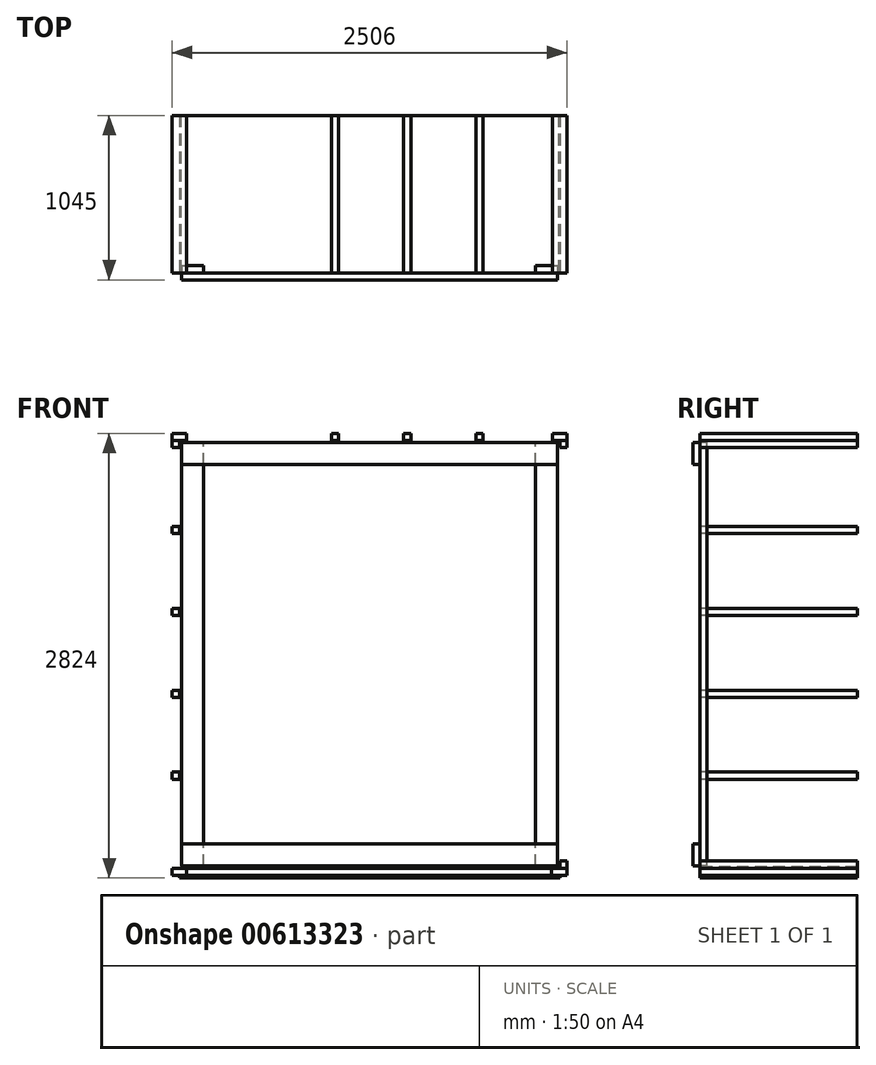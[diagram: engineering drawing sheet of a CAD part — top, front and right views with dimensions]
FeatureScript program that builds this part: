
annotation { "Feature Type Name" : "Feature", "Feature Type Description" : "" }
export const myFeature = defineFeature(function(context is Context, id is Id, definition is map)
    precondition{}
    {
        {
            var Q0;
            Q0=qCreatedBy(makeId("Front.planeOp"),FACE);
            var sketch = newSketch(context, id + "F0", { "sketchPlane" : qUnion([Q0])});
            skLineSegment(sketch, "E0.bottom", {"start": v(0, 0) * mm, "end": v(2400, 0) * mm});
            skLineSegment(sketch, "E0.top", {"start": v(0, 2700) * mm, "end": v(2400, 2700) * mm});
            skLineSegment(sketch, "E0.left", {"start": v(0, 0) * mm, "end": v(0, 2700) * mm});
            skLineSegment(sketch, "E0.right", {"start": v(2400, 0) * mm, "end": v(2400, 2700) * mm});
            skLineSegment(sketch, "E1.0", {"start": v(145, 2555) * mm, "end": v(2255, 2555) * mm});
            skLineSegment(sketch, "E1.1", {"start": v(145, 145) * mm, "end": v(145, 2555) * mm});
            skLineSegment(sketch, "E1.2", {"start": v(145, 145) * mm, "end": v(2255, 145) * mm});
            skLineSegment(sketch, "E1.3", {"start": v(2255, 145) * mm, "end": v(2255, 2555) * mm});
            skLineSegment(sketch, "E2.0", {"start": v(167, 167) * mm, "end": v(167, 2533) * mm});
            skLineSegment(sketch, "E2.1", {"start": v(167, 167) * mm, "end": v(2233, 167) * mm});
            skLineSegment(sketch, "E2.2", {"start": v(2233, 167) * mm, "end": v(2233, 2533) * mm});
            skLineSegment(sketch, "E2.3", {"start": v(167, 2533) * mm, "end": v(2233, 2533) * mm});
            skLineSegment(sketch, "E3", {"start": v(145, 2555) * mm, "end": v(0, 2555) * mm});
            skLineSegment(sketch, "E4", {"start": v(145, 2555) * mm, "end": v(145, 2700) * mm});
            skLineSegment(sketch, "E5", {"start": v(2255, 2555) * mm, "end": v(2255, 2700) * mm});
            skLineSegment(sketch, "E6", {"start": v(2255, 2555) * mm, "end": v(2400, 2555) * mm});
            skLineSegment(sketch, "E7", {"start": v(145, 145) * mm, "end": v(145, 0) * mm});
            skLineSegment(sketch, "E8", {"start": v(145, 145) * mm, "end": v(0, 145) * mm});
            skLineSegment(sketch, "E9", {"start": v(2255, 145) * mm, "end": v(2400, 145) * mm});
            skLineSegment(sketch, "E10", {"start": v(2255, 145) * mm, "end": v(2255, 0) * mm});
            skLineSegment(sketch, "E11.0", {"start": v(5, 2695) * mm, "end": v(2395, 2695) * mm});
            skLineSegment(sketch, "E11.1", {"start": v(5, 5) * mm, "end": v(5, 2695) * mm});
            skLineSegment(sketch, "E11.2", {"start": v(5, 5) * mm, "end": v(2395, 5) * mm});
            skLineSegment(sketch, "E11.3", {"start": v(2395, 5) * mm, "end": v(2395, 2695) * mm});
            skLineSegment(sketch, "E12.0", {"start": v(-8, 2708) * mm, "end": v(2408, 2708) * mm});
            skLineSegment(sketch, "E12.1", {"start": v(-8, -8) * mm, "end": v(-8, 2708) * mm});
            skLineSegment(sketch, "E12.2", {"start": v(-8, -8) * mm, "end": v(2408, -8) * mm});
            skLineSegment(sketch, "E12.3", {"start": v(2408, -8) * mm, "end": v(2408, 2708) * mm});
            skLineSegment(sketch, "E13", {"start": v(0, 2700) * mm, "end": v(0, 2708) * mm});
            skLineSegment(sketch, "E14", {"start": v(2400, 2700) * mm, "end": v(2400, 2708) * mm});
            skLineSegment(sketch, "E15", {"start": v(2400, 0) * mm, "end": v(2400, -8) * mm});
            skLineSegment(sketch, "E16", {"start": v(0, 0) * mm, "end": v(0, -8) * mm});
            skLineSegment(sketch, "E17.bottom", {"start": v(-53, -8) * mm, "end": v(37, -8) * mm});
            skLineSegment(sketch, "E17.top", {"start": v(-53, -53) * mm, "end": v(37, -53) * mm});
            skLineSegment(sketch, "E17.left", {"start": v(-53, -8) * mm, "end": v(-53, -53) * mm});
            skLineSegment(sketch, "E17.right", {"start": v(37, -8) * mm, "end": v(37, -53) * mm});
            skLineSegment(sketch, "E18.bottom", {"start": v(2408, -8) * mm, "end": v(2354.44, -8) * mm});
            skLineSegment(sketch, "E18.top", {"start": v(2408, -53) * mm, "end": v(2354.44, -53) * mm});
            skLineSegment(sketch, "E18.left", {"start": v(2408, -8) * mm, "end": v(2408, -53) * mm});
            skLineSegment(sketch, "E18.right", {"start": v(2354.44, -8) * mm, "end": v(2354.44, -53) * mm});
            skLineSegment(sketch, "E19.bottom", {"start": v(2408, 37) * mm, "end": v(2453, 37) * mm});
            skLineSegment(sketch, "E19.top", {"start": v(2408, -53) * mm, "end": v(2453, -53) * mm});
            skLineSegment(sketch, "E19.left", {"start": v(2408, 37) * mm, "end": v(2408, -53) * mm});
            skLineSegment(sketch, "E19.right", {"start": v(2453, 37) * mm, "end": v(2453, -53) * mm});
            skLineSegment(sketch, "E20", {"start": v(2408, -8) * mm, "end": v(2453, -8) * mm});
            skLineSegment(sketch, "E21.bottom", {"start": v(-8, -8) * mm, "end": v(-53, -8) * mm});
            skLineSegment(sketch, "E21.top", {"start": v(-8, 37) * mm, "end": v(-53, 37) * mm});
            skLineSegment(sketch, "E21.left", {"start": v(-8, -8) * mm, "end": v(-8, 37) * mm});
            skLineSegment(sketch, "E21.right", {"start": v(-53, -8) * mm, "end": v(-53, 37) * mm});
            skLineSegment(sketch, "E22.bottom", {"start": v(-8, 2708) * mm, "end": v(37, 2708) * mm});
            skLineSegment(sketch, "E22.top", {"start": v(-8, 2753) * mm, "end": v(37, 2753) * mm});
            skLineSegment(sketch, "E22.left", {"start": v(-8, 2708) * mm, "end": v(-8, 2753) * mm});
            skLineSegment(sketch, "E22.right", {"start": v(37, 2708) * mm, "end": v(37, 2753) * mm});
            skLineSegment(sketch, "E23.bottom", {"start": v(-8, 2753) * mm, "end": v(-53, 2753) * mm});
            skLineSegment(sketch, "E23.top", {"start": v(-8, 2663) * mm, "end": v(-53, 2663) * mm});
            skLineSegment(sketch, "E23.left", {"start": v(-8, 2753) * mm, "end": v(-8, 2663) * mm});
            skLineSegment(sketch, "E23.right", {"start": v(-53, 2753) * mm, "end": v(-53, 2663) * mm});
            skLineSegment(sketch, "E24", {"start": v(-8, 2708) * mm, "end": v(-53, 2708) * mm});
            skLineSegment(sketch, "E25.bottom", {"start": v(2408, 2708) * mm, "end": v(2363, 2708) * mm});
            skLineSegment(sketch, "E25.top", {"start": v(2408, 2753) * mm, "end": v(2363, 2753) * mm});
            skLineSegment(sketch, "E25.left", {"start": v(2408, 2708) * mm, "end": v(2408, 2753) * mm});
            skLineSegment(sketch, "E25.right", {"start": v(2363, 2708) * mm, "end": v(2363, 2753) * mm});
            skLineSegment(sketch, "E26.bottom", {"start": v(2408, 2753) * mm, "end": v(2453, 2753) * mm});
            skLineSegment(sketch, "E26.top", {"start": v(2408, 2663) * mm, "end": v(2453, 2663) * mm});
            skLineSegment(sketch, "E26.left", {"start": v(2408, 2753) * mm, "end": v(2408, 2663) * mm});
            skLineSegment(sketch, "E26.right", {"start": v(2453, 2753) * mm, "end": v(2453, 2663) * mm});
            skLineSegment(sketch, "E27", {"start": v(2408, 2708) * mm, "end": v(2453, 2708) * mm});
            skLineSegment(sketch, "E28.bottom", {"start": v(37, -53) * mm, "end": v(2354.44, -53) * mm});
            skLineSegment(sketch, "E28.top", {"start": v(37, -8) * mm, "end": v(2354.44, -8) * mm});
            skLineSegment(sketch, "E28.left", {"start": v(37, -53) * mm, "end": v(37, -8) * mm});
            skLineSegment(sketch, "E28.right", {"start": v(2354.44, -53) * mm, "end": v(2354.44, -8) * mm});
            skPoint(sketch, "E29.oppositeSnap0", {"position": v(2408, -30.5) * mm});
            skLineSegment(sketch, "E29.bottom", {"start": v(-8, -53) * mm, "end": v(2408, -53) * mm});
            skLineSegment(sketch, "E29.top", {"start": v(-8, -71) * mm, "end": v(2408, -71) * mm});
            skLineSegment(sketch, "E29.left", {"start": v(-8, -53) * mm, "end": v(-8, -71) * mm});
            skLineSegment(sketch, "E29.right", {"start": v(2408, -53) * mm, "end": v(2408, -71) * mm});
            skLineSegment(sketch, "E30.bottom", {"start": v(497, 2708) * mm, "end": v(542, 2708) * mm});
            skLineSegment(sketch, "E30.top", {"start": v(497, 2753) * mm, "end": v(542, 2753) * mm});
            skLineSegment(sketch, "E30.left", {"start": v(497, 2708) * mm, "end": v(497, 2753) * mm});
            skLineSegment(sketch, "E30.right", {"start": v(542, 2708) * mm, "end": v(542, 2753) * mm});
            skLineSegment(sketch, "E31.1.0.0", {"start": v(957, 2708) * mm, "end": v(957, 2753) * mm});
            skLineSegment(sketch, "E31.1.0.1", {"start": v(957, 2753) * mm, "end": v(1002, 2753) * mm});
            skLineSegment(sketch, "E31.1.0.2", {"start": v(1002, 2708) * mm, "end": v(1002, 2753) * mm});
            skLineSegment(sketch, "E31.2.0.0", {"start": v(1417, 2708) * mm, "end": v(1417, 2753) * mm});
            skLineSegment(sketch, "E31.2.0.1", {"start": v(1417, 2753) * mm, "end": v(1462, 2753) * mm});
            skLineSegment(sketch, "E31.2.0.2", {"start": v(1462, 2708) * mm, "end": v(1462, 2753) * mm});
            skLineSegment(sketch, "E31.3.0.0", {"start": v(1877, 2708) * mm, "end": v(1877, 2753) * mm});
            skLineSegment(sketch, "E31.3.0.1", {"start": v(1877, 2753) * mm, "end": v(1922, 2753) * mm});
            skLineSegment(sketch, "E31.3.0.2", {"start": v(1922, 2708) * mm, "end": v(1922, 2753) * mm});
            skLineSegment(sketch, "E31.direction1", {"start": v(497, 2708) * mm, "end": v(957, 2708) * mm, "construction": true});
            skLineSegment(sketch, "E32.bottom", {"start": v(-8, 557) * mm, "end": v(-53, 557) * mm});
            skLineSegment(sketch, "E32.top", {"start": v(-8, 602) * mm, "end": v(-53, 602) * mm});
            skLineSegment(sketch, "E32.left", {"start": v(-8, 557) * mm, "end": v(-8, 602) * mm});
            skLineSegment(sketch, "E32.right", {"start": v(-53, 557) * mm, "end": v(-53, 602) * mm});
            skLineSegment(sketch, "E33.0.1.0", {"start": v(-8, 1077) * mm, "end": v(-53, 1077) * mm});
            skLineSegment(sketch, "E33.0.1.1", {"start": v(-53, 1077) * mm, "end": v(-53, 1122) * mm});
            skLineSegment(sketch, "E33.0.1.2", {"start": v(-8, 1122) * mm, "end": v(-53, 1122) * mm});
            skLineSegment(sketch, "E33.0.2.0", {"start": v(-8, 1597) * mm, "end": v(-53, 1597) * mm});
            skLineSegment(sketch, "E33.0.2.1", {"start": v(-53, 1597) * mm, "end": v(-53, 1642) * mm});
            skLineSegment(sketch, "E33.0.2.2", {"start": v(-8, 1642) * mm, "end": v(-53, 1642) * mm});
            skLineSegment(sketch, "E33.0.3.0", {"start": v(-8, 2117) * mm, "end": v(-53, 2117) * mm});
            skLineSegment(sketch, "E33.0.3.1", {"start": v(-53, 2117) * mm, "end": v(-53, 2162) * mm});
            skLineSegment(sketch, "E33.0.3.2", {"start": v(-8, 2162) * mm, "end": v(-53, 2162) * mm});
            skLineSegment(sketch, "E33.direction1", {"start": v(-53, 557) * mm, "end": v(-28, 557) * mm, "construction": true});
            skLineSegment(sketch, "E33.direction2", {"start": v(-53, 557) * mm, "end": v(-53, 1077) * mm, "construction": true});
            skSolve(sketch);
        }
        {
            var Q0;
            {var subQ4=sQuery(id+"F0.wireOp",EDGE,"E3");Q0=makeQuery(id+"F0.imprint","IMPRINT",FACE,{"disambiguationData":[TD([[makeQuery(id+"F0.imprint","IMPRINT",EDGE,{"derivedFrom":subQ4}),-1.0]])]});}
            var Q1;
            Q1=makeQuery(id+"F0.imprint","IMPRINT",FACE,{"disambiguationData":[TD([[makeQuery(id+"F0.imprint","IMPRINT",EDGE,{"derivedFrom":sQuery(id+"F0.wireOp",EDGE,"E1.1")}),1.0]])]});
            var Q2;
            {var subQ3=sQuery(id+"F0.wireOp",EDGE,"E7");Q2=makeQuery(id+"F0.imprint","IMPRINT",FACE,{"disambiguationData":[TD([[makeQuery(id+"F0.imprint","IMPRINT",EDGE,{"derivedFrom":subQ3}),-1.0]])]});}
            var Q3;
            {var subQ3=sQuery(id+"F0.wireOp",EDGE,"E5");Q3=makeQuery(id+"F0.imprint","IMPRINT",FACE,{"disambiguationData":[TD([[makeQuery(id+"F0.imprint","IMPRINT",EDGE,{"derivedFrom":subQ3}),-1.0]])]});}
            var Q4;
            Q4=makeQuery(id+"F0.imprint","IMPRINT",FACE,{"disambiguationData":[TD([[makeQuery(id+"F0.imprint","IMPRINT",EDGE,{"derivedFrom":sQuery(id+"F0.wireOp",EDGE,"E1.3")}),-1.0]])]});
            var Q5;
            {var subQ4=sQuery(id+"F0.wireOp",EDGE,"E9");Q5=makeQuery(id+"F0.imprint","IMPRINT",FACE,{"disambiguationData":[TD([[makeQuery(id+"F0.imprint","IMPRINT",EDGE,{"derivedFrom":subQ4}),-1.0]])]});}
            extrude(context, id + "F1", {"entities" : qUnion([Q0, Q1, Q2, Q3, Q4, Q5]), "depth" : -45 * mm, "offsetDistance" : 25 * mm});
        }
        {
            var Q0;
            Q0=makeQuery(id+"F0.imprint","IMPRINT",FACE,{"disambiguationData":[TD([[makeQuery(id+"F0.imprint","IMPRINT",EDGE,{"derivedFrom":sQuery(id+"F0.wireOp",EDGE,"E1.0")}),1.0]])]});
            var Q1;
            {var subQ4=sQuery(id+"F0.wireOp",EDGE,"E3");Q1=makeQuery(id+"F0.imprint","IMPRINT",FACE,{"disambiguationData":[TD([[makeQuery(id+"F0.imprint","IMPRINT",EDGE,{"derivedFrom":subQ4}),-1.0]])]});}
            var Q2;
            {var subQ3=sQuery(id+"F0.wireOp",EDGE,"E5");Q2=makeQuery(id+"F0.imprint","IMPRINT",FACE,{"disambiguationData":[TD([[makeQuery(id+"F0.imprint","IMPRINT",EDGE,{"derivedFrom":subQ3}),-1.0]])]});}
            var Q3;
            {var subQ3=sQuery(id+"F0.wireOp",EDGE,"E7");Q3=makeQuery(id+"F0.imprint","IMPRINT",FACE,{"disambiguationData":[TD([[makeQuery(id+"F0.imprint","IMPRINT",EDGE,{"derivedFrom":subQ3}),-1.0]])]});}
            var Q4;
            Q4=makeQuery(id+"F0.imprint","IMPRINT",FACE,{"disambiguationData":[TD([[makeQuery(id+"F0.imprint","IMPRINT",EDGE,{"derivedFrom":sQuery(id+"F0.wireOp",EDGE,"E1.2")}),-1.0]])]});
            var Q5;
            {var subQ4=sQuery(id+"F0.wireOp",EDGE,"E9");Q5=makeQuery(id+"F0.imprint","IMPRINT",FACE,{"disambiguationData":[TD([[makeQuery(id+"F0.imprint","IMPRINT",EDGE,{"derivedFrom":subQ4}),-1.0]])]});}
            extrude(context, id + "F2", {"entities" : qUnion([Q0, Q1, Q2, Q3, Q4, Q5]), "depth" : 45 * mm, "offsetDistance" : 25 * mm});
        }
        {
            var Q0;
            {var subQ0=sQuery(id+"F0.wireOp",EDGE,"E23.bottom");Q0=makeQuery(id+"F0.imprint","IMPRINT",FACE,{"disambiguationData":[TD([[makeQuery(id+"F0.imprint","IMPRINT",EDGE,{"derivedFrom":subQ0}),1.0]])]});}
            var Q1;
            {var subQ1=sQuery(id+"F0.wireOp",EDGE,"E22.top");Q1=makeQuery(id+"F0.imprint","IMPRINT",FACE,{"disambiguationData":[TD([[makeQuery(id+"F0.imprint","IMPRINT",EDGE,{"derivedFrom":subQ1}),-1.0]])]});}
            var Q2;
            {var subQ1=sQuery(id+"F0.wireOp",EDGE,"E25.top");Q2=makeQuery(id+"F0.imprint","IMPRINT",FACE,{"disambiguationData":[TD([[makeQuery(id+"F0.imprint","IMPRINT",EDGE,{"derivedFrom":subQ1}),1.0]])]});}
            var Q3;
            {var subQ0=sQuery(id+"F0.wireOp",EDGE,"E26.bottom");Q3=makeQuery(id+"F0.imprint","IMPRINT",FACE,{"disambiguationData":[TD([[makeQuery(id+"F0.imprint","IMPRINT",EDGE,{"derivedFrom":subQ0}),-1.0]])]});}
            var Q4;
            {var subQ0=sQuery(id+"F0.wireOp",EDGE,"E18.top");Q4=makeQuery(id+"F0.imprint","IMPRINT",FACE,{"disambiguationData":[TD([[makeQuery(id+"F0.imprint","IMPRINT",EDGE,{"derivedFrom":subQ0}),-1.0]])]});}
            var Q5;
            {var subQ0=sQuery(id+"F0.wireOp",EDGE,"E19.top");Q5=makeQuery(id+"F0.imprint","IMPRINT",FACE,{"disambiguationData":[TD([[makeQuery(id+"F0.imprint","IMPRINT",EDGE,{"derivedFrom":subQ0}),1.0]])]});}
            var Q6;
            Q6=makeQuery(id+"F0.imprint","IMPRINT",FACE,{"disambiguationData":[TD([[makeQuery(id+"F0.imprint","IMPRINT",EDGE,{"derivedFrom":sQuery(id+"F0.wireOp",EDGE,"E17.top")}),1.0]])]});
            extrude(context, id + "F3", {"entities" : qUnion([Q0, Q1, Q2, Q3, Q4, Q5, Q6]), "depth" : -1000 * mm, "offsetDistance" : 25 * mm});
        }
        {
            var Q0;
            {var subQ0=sQuery(id+"F0.wireOp",EDGE,"E23.top");Q0=makeQuery(id+"F0.imprint","IMPRINT",FACE,{"disambiguationData":[TD([[makeQuery(id+"F0.imprint","IMPRINT",EDGE,{"derivedFrom":subQ0}),-1.0]])]});}
            var Q1;
            {var subQ0=sQuery(id+"F0.wireOp",EDGE,"E26.top");Q1=makeQuery(id+"F0.imprint","IMPRINT",FACE,{"disambiguationData":[TD([[makeQuery(id+"F0.imprint","IMPRINT",EDGE,{"derivedFrom":subQ0}),1.0]])]});}
            var Q2;
            {var subQ0=sQuery(id+"F0.wireOp",EDGE,"E19.bottom");Q2=makeQuery(id+"F0.imprint","IMPRINT",FACE,{"disambiguationData":[TD([[makeQuery(id+"F0.imprint","IMPRINT",EDGE,{"derivedFrom":subQ0}),-1.0]])]});}
            var Q3;
            Q3=makeQuery(id+"F0.imprint","IMPRINT",FACE,{"disambiguationData":[TD([[makeQuery(id+"F0.imprint","IMPRINT",EDGE,{"derivedFrom":sQuery(id+"F0.wireOp",EDGE,"E21.bottom")}),-1.0]])]});
            extrude(context, id + "F4", {"entities" : qUnion([Q0, Q1, Q2, Q3]), "depth" : -1000 * mm, "offsetDistance" : 25 * mm});
        }
        {
            var Q0;
            Q0=makeQuery(id+"F0.imprint","IMPRINT",FACE,{"disambiguationData":[TD([[makeQuery(id+"F0.imprint","IMPRINT",EDGE,{"derivedFrom":sQuery(id+"F0.wireOp",EDGE,"E29.top")}),1.0]])]});
            extrude(context, id + "F5", {"entities" : qUnion([Q0]), "depth" : -1000 * mm, "offsetDistance" : 25 * mm});
        }
        {
            var Q0;
            {var subQ0=sQuery(id+"F0.wireOp",EDGE,"E15");Q0=makeQuery(id+"F0.imprint","IMPRINT",FACE,{"disambiguationData":[TD([[makeQuery(id+"F0.imprint","IMPRINT",EDGE,{"derivedFrom":subQ0}),-1.0]])]});}
            extrude(context, id + "F6", {"entities" : qUnion([Q0]), "depth" : -1000 * mm, "offsetDistance" : 25 * mm});
        }
        {
            var Q0;
            Q0=makeQuery(id+"F0.imprint","IMPRINT",FACE,{"disambiguationData":[TD([[makeQuery(id+"F0.imprint","IMPRINT",EDGE,{"derivedFrom":sQuery(id+"F0.wireOp",EDGE,"E30.bottom")}),1.0]])]});
            var Q1;
            {var subQ0=sQuery(id+"F0.wireOp",EDGE,"E31.1.0.0");Q1=makeQuery(id+"F0.imprint","IMPRINT",FACE,{"disambiguationData":[TD([[makeQuery(id+"F0.imprint","IMPRINT",EDGE,{"derivedFrom":subQ0}),-1.0]])]});}
            var Q2;
            {var subQ0=sQuery(id+"F0.wireOp",EDGE,"E31.2.0.0");Q2=makeQuery(id+"F0.imprint","IMPRINT",FACE,{"disambiguationData":[TD([[makeQuery(id+"F0.imprint","IMPRINT",EDGE,{"derivedFrom":subQ0}),-1.0]])]});}
            var Q3;
            {var subQ0=sQuery(id+"F0.wireOp",EDGE,"E31.3.0.0");Q3=makeQuery(id+"F0.imprint","IMPRINT",FACE,{"disambiguationData":[TD([[makeQuery(id+"F0.imprint","IMPRINT",EDGE,{"derivedFrom":subQ0}),-1.0]])]});}
            extrude(context, id + "F7", {"entities" : qUnion([Q0, Q1, Q2, Q3]), "depth" : -1000 * mm, "offsetDistance" : 25 * mm});
        }
        {
            var Q0;
            Q0=makeQuery(id+"F0.imprint","IMPRINT",FACE,{"disambiguationData":[TD([[makeQuery(id+"F0.imprint","IMPRINT",EDGE,{"derivedFrom":sQuery(id+"F0.wireOp",EDGE,"E32.bottom")}),-1.0]])]});
            var Q1;
            {var subQ0=sQuery(id+"F0.wireOp",EDGE,"E33.0.1.0");Q1=makeQuery(id+"F0.imprint","IMPRINT",FACE,{"disambiguationData":[TD([[makeQuery(id+"F0.imprint","IMPRINT",EDGE,{"derivedFrom":subQ0}),-1.0]])]});}
            var Q2;
            {var subQ0=sQuery(id+"F0.wireOp",EDGE,"E33.0.2.0");Q2=makeQuery(id+"F0.imprint","IMPRINT",FACE,{"disambiguationData":[TD([[makeQuery(id+"F0.imprint","IMPRINT",EDGE,{"derivedFrom":subQ0}),-1.0]])]});}
            var Q3;
            {var subQ0=sQuery(id+"F0.wireOp",EDGE,"E33.0.3.0");Q3=makeQuery(id+"F0.imprint","IMPRINT",FACE,{"disambiguationData":[TD([[makeQuery(id+"F0.imprint","IMPRINT",EDGE,{"derivedFrom":subQ0}),-1.0]])]});}
            extrude(context, id + "F8", {"entities" : qUnion([Q0, Q1, Q2, Q3]), "depth" : -1000 * mm, "offsetDistance" : 25 * mm});
        }
    });
